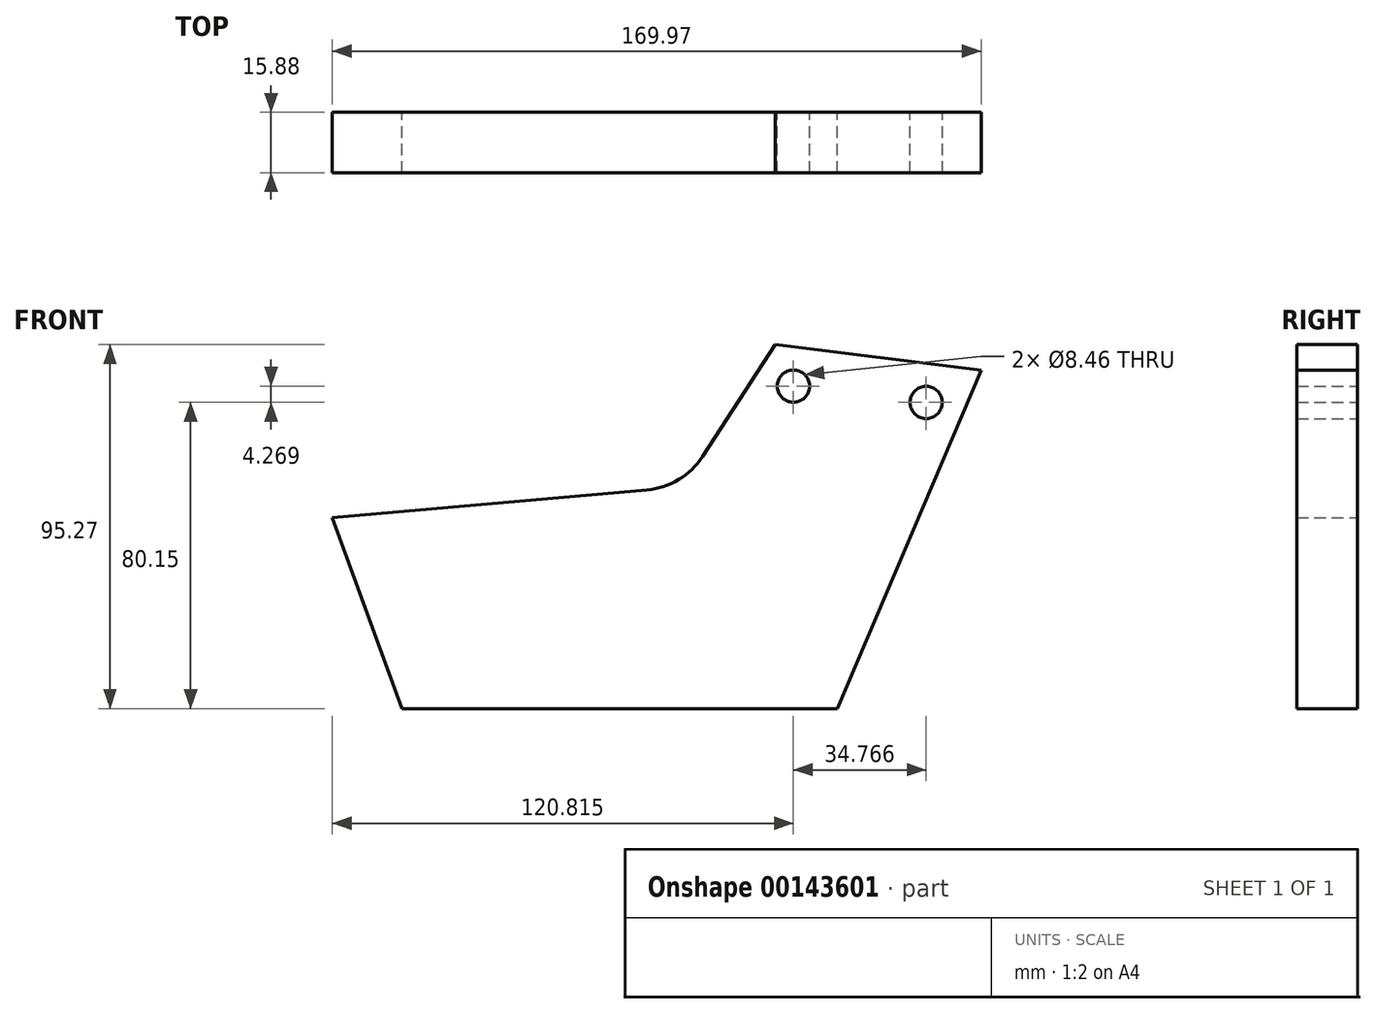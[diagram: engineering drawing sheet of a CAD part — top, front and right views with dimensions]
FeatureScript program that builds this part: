
annotation { "Feature Type Name" : "Feature", "Feature Type Description" : "" }
export const myFeature = defineFeature(function(context is Context, id is Id, definition is map)
    precondition{}
    {
        {
            var Q0;
            Q0=qCreatedBy(makeId("Front.planeOp"),FACE);
            var sketch = newSketch(context, id + "F0", { "sketchPlane" : qUnion([Q0])});
            skCircle(sketch, "E0", {"center": v(0, 0) * mm, "radius": 4.23 * mm});
            skCircle(sketch, "E1", {"center": v(-34.77, 4.27) * mm, "radius": 4.23 * mm});
            skLineSegment(sketch, "E2", {"start": v(-39.56, 15.12) * mm, "end": v(14.4, 8.5) * mm});
            skLineSegment(sketch, "E3", {"start": v(14.4, 8.5) * mm, "end": v(-23.23, -80.15) * mm});
            skLineSegment(sketch, "E4", {"start": v(-23.23, -80.15) * mm, "end": v(-137.37, -80.15) * mm});
            skLineSegment(sketch, "E5", {"start": v(-137.37, -80.15) * mm, "end": v(-155.58, -30.11) * mm});
            skLineSegment(sketch, "E6", {"start": v(-155.58, -30.11) * mm, "end": v(-73.16, -22.9) * mm});
            skArc(sketch, "E7", {"start": v(-73.16, -22.9) * mm, "mid": v(-64.84, -20.2) * mm, "end": v(-58.55, -14.13) * mm});
            skLineSegment(sketch, "E8", {"start": v(-58.55, -14.13) * mm, "end": v(-39.56, 15.12) * mm});
            skLineSegment(sketch, "E9", {"start": v(0, 0) * mm, "end": v(0, 48.12) * mm, "construction": true});
            skSolve(sketch);
        }
        {
            var Q0;
            Q0=makeQuery(id+"F0.imprint","IMPRINT",FACE,{"disambiguationData":[TD([[makeQuery(id+"F0.imprint","IMPRINT",EDGE,{"derivedFrom":sQuery(id+"F0.wireOp",EDGE,"E0")}),-1.0]])]});
            extrude(context, id + "F1", {"entities" : qUnion([Q0]), "depth" : 15.88 * mm});
        }
        {
            var Q0;
            Q0=makeQuery(id+"F1.opExtrude","CAP_FACE",FACE,{"disambiguationData":[OSD([sQuery(id+"F0.wireOp",EDGE,"E0"),sQuery(id+"F0.wireOp",EDGE,"E1"),sQuery(id+"F0.wireOp",EDGE,"E2"),sQuery(id+"F0.wireOp",EDGE,"E3"),sQuery(id+"F0.wireOp",EDGE,"E4"),sQuery(id+"F0.wireOp",EDGE,"E5"),sQuery(id+"F0.wireOp",EDGE,"E6"),sQuery(id+"F0.wireOp",EDGE,"E7"),sQuery(id+"F0.wireOp",EDGE,"E8")])],"isStart":false});
            var sketch = newSketch(context, id + "F2", { "sketchPlane" : qUnion([Q0])});
            skLineSegment(sketch, "E10.0", {"start": v(-153.29, -36.41) * mm, "end": v(-8.06, -23.7) * mm});
            skArc(sketch, "E11", {"start": v(-8.06, -23.7) * mm, "mid": v(-0.43, -20.86) * mm, "end": v(4.64, -14.48) * mm});
            skSolve(sketch);
        }
        {
            var Q0;
            Q0 = qSketchRegion(id + "F2", true);
            var Q1;
            {var subQ2=sQuery(id+"F2.wireOp",EDGE,"E10.0");Q1=makeQuery(id+"F2.imprint","IMPRINT",FACE,{"disambiguationData":[TD([[makeQuery(id+"F2.imprint","IMPRINT",EDGE,{"derivedFrom":subQ2}),-1.0]])]});}
            extrude(context, id + "F3", {"entities" : qUnion([Q0, Q1]), "operationType" : NewBodyOperationType.REMOVE, "oppositeDirection" : true, "depth" : 10.3 * mm});
        }
        {
            var Q0;
            Q0=makeQuery(id+"F1.opExtrude","CAP_FACE",FACE,{"disambiguationData":[OSD([sQuery(id+"F0.wireOp",EDGE,"E0"),sQuery(id+"F0.wireOp",EDGE,"E1"),sQuery(id+"F0.wireOp",EDGE,"E2"),sQuery(id+"F0.wireOp",EDGE,"E3"),sQuery(id+"F0.wireOp",EDGE,"E4"),sQuery(id+"F0.wireOp",EDGE,"E5"),sQuery(id+"F0.wireOp",EDGE,"E6"),sQuery(id+"F0.wireOp",EDGE,"E7"),sQuery(id+"F0.wireOp",EDGE,"E8")])],"isStart":false});
            var sketch = newSketch(context, id + "F4", { "sketchPlane" : qUnion([Q0])});
            skCircle(sketch, "E12", {"center": v(-25.72, -6.47) * mm, "radius": 6.88 * mm});
            skSolve(sketch);
        }
        {
            var Q0;
            Q0=makeQuery(id+"F0.imprint","IMPRINT",FACE,{"disambiguationData":[TD([[makeQuery(id+"F0.imprint","IMPRINT",EDGE,{"derivedFrom":sQuery(id+"F0.wireOp",EDGE,"E0")}),-1.0]])]});
            extrude(context, id + "F5", {"entities" : qUnion([Q0]), "operationType" : NewBodyOperationType.ADD, "depth" : 15.88 * mm});
        }
        {
            var Q0;
            Q0=makeQuery(id+"F0.imprint","IMPRINT",FACE,{"disambiguationData":[TD([[makeQuery(id+"F0.imprint","IMPRINT",EDGE,{"derivedFrom":sQuery(id+"F0.wireOp",EDGE,"E0")}),-1.0]])]});
            extrude(context, id + "F6", {"entities" : qUnion([Q0]), "operationType" : NewBodyOperationType.ADD, "depth" : 15.88 * mm});
        }
    });
